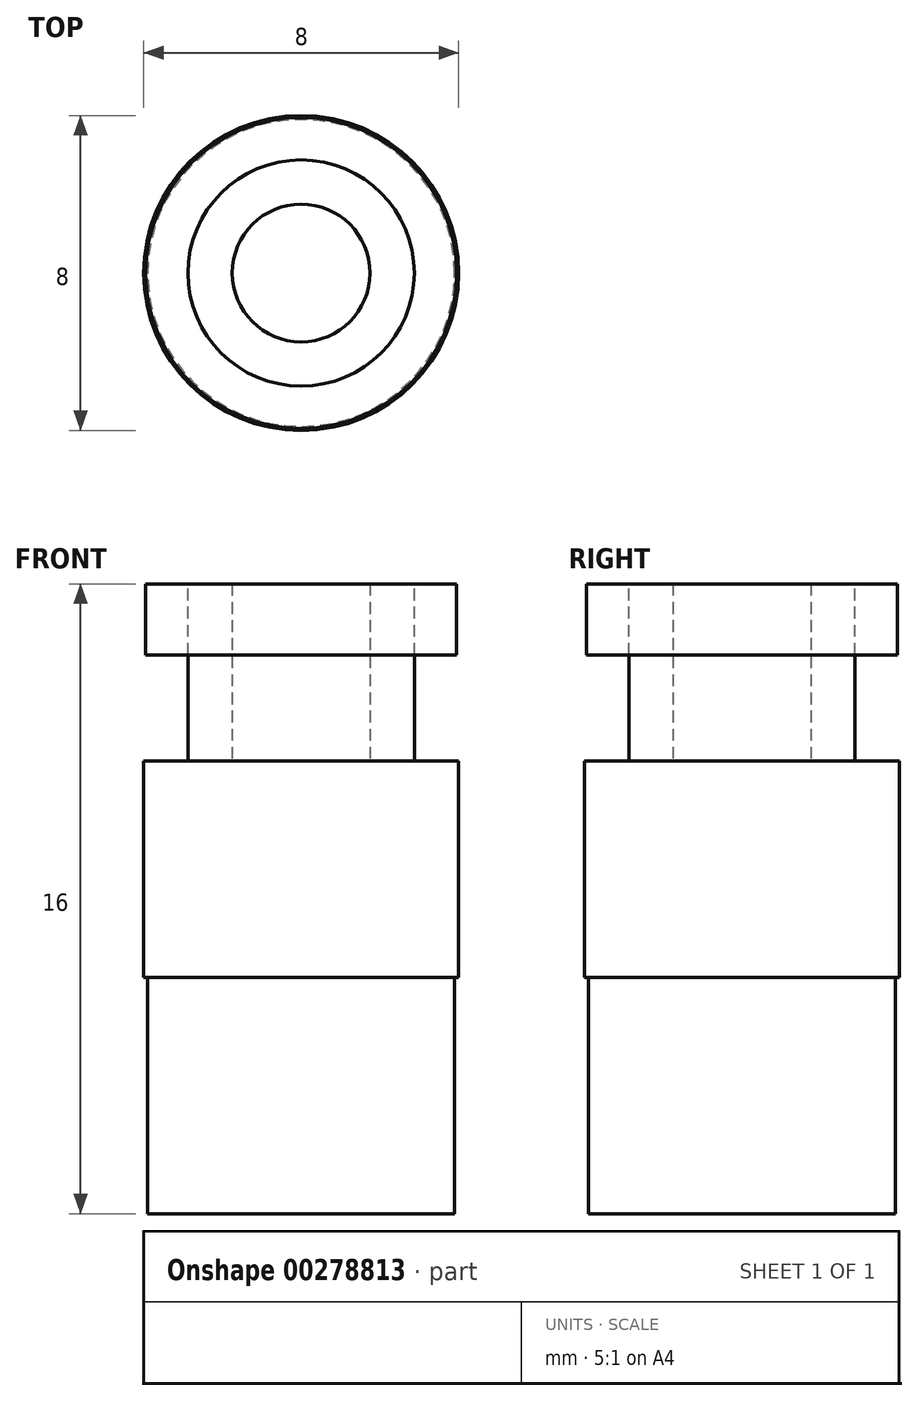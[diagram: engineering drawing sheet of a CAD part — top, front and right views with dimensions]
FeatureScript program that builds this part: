
annotation { "Feature Type Name" : "Feature", "Feature Type Description" : "" }
export const myFeature = defineFeature(function(context is Context, id is Id, definition is map)
    precondition{}
    {
        {
            var Q0;
            Q0=qCreatedBy(makeId("Top.planeOp"),FACE);
            var sketch = newSketch(context, id + "F0", { "sketchPlane" : qUnion([Q0])});
            skCircle(sketch, "E0", {"center": v(0, 0) * mm, "radius": 4 * mm});
            skSolve(sketch);
        }
        {
            var Q0;
            Q0 = qSketchRegion(id + "F0", true);
            extrude(context, id + "F1", {"entities" : qUnion([Q0]), "depth" : 5.5 * mm});
        }
        {
            var Q0;
            Q0=makeQuery(id+"F1.opExtrude","CAP_FACE",FACE,{"disambiguationData":[OSD([sQuery(id+"F0.wireOp",EDGE,"E0")])],"isStart":true});
            var sketch = newSketch(context, id + "F2", { "sketchPlane" : qUnion([Q0])});
            skCircle(sketch, "E1", {"center": v(0, 0) * mm, "radius": 3.9 * mm});
            skSolve(sketch);
        }
        {
            var Q0;
            Q0 = qSketchRegion(id + "F2", true);
            extrude(context, id + "F3", {"entities" : qUnion([Q0]), "depth" : 6 * mm});
        }
        {
            var Q0;
            Q0=makeQuery(id+"F1.opExtrude","CAP_FACE",FACE,{"disambiguationData":[OSD([sQuery(id+"F0.wireOp",EDGE,"E0")])],"isStart":false});
            var sketch = newSketch(context, id + "F4", { "sketchPlane" : qUnion([Q0])});
            skCircle(sketch, "E2", {"center": v(0, 0) * mm, "radius": 2.88 * mm});
            skCircle(sketch, "E3", {"center": v(0, 0) * mm, "radius": 1.75 * mm});
            skSolve(sketch);
        }
        {
            var Q0;
            Q0 = qSketchRegion(id + "F4", true);
            extrude(context, id + "F5", {"entities" : qUnion([Q0]), "operationType" : NewBodyOperationType.ADD, "depth" : 4.5 * mm});
        }
        {
            var Q0;
            Q0=makeQuery(id+"F5.opExtrude","CAP_FACE",FACE,{"disambiguationData":[OSD([sQuery(id+"F4.wireOp",EDGE,"E2"),sQuery(id+"F4.wireOp",EDGE,"E3")])],"isStart":false});
            var sketch = newSketch(context, id + "F6", { "sketchPlane" : qUnion([Q0])});
            skCircle(sketch, "E4", {"center": v(0, 0) * mm, "radius": 3.95 * mm});
            skCircle(sketch, "E5.0", {"center": v(0, 0) * mm, "radius": 2.88 * mm});
            skSolve(sketch);
        }
        {
            var Q0;
            Q0 = qSketchRegion(id + "F6", true);
            extrude(context, id + "F7", {"entities" : qUnion([Q0]), "oppositeDirection" : true, "depth" : 1.8 * mm});
        }
    });
